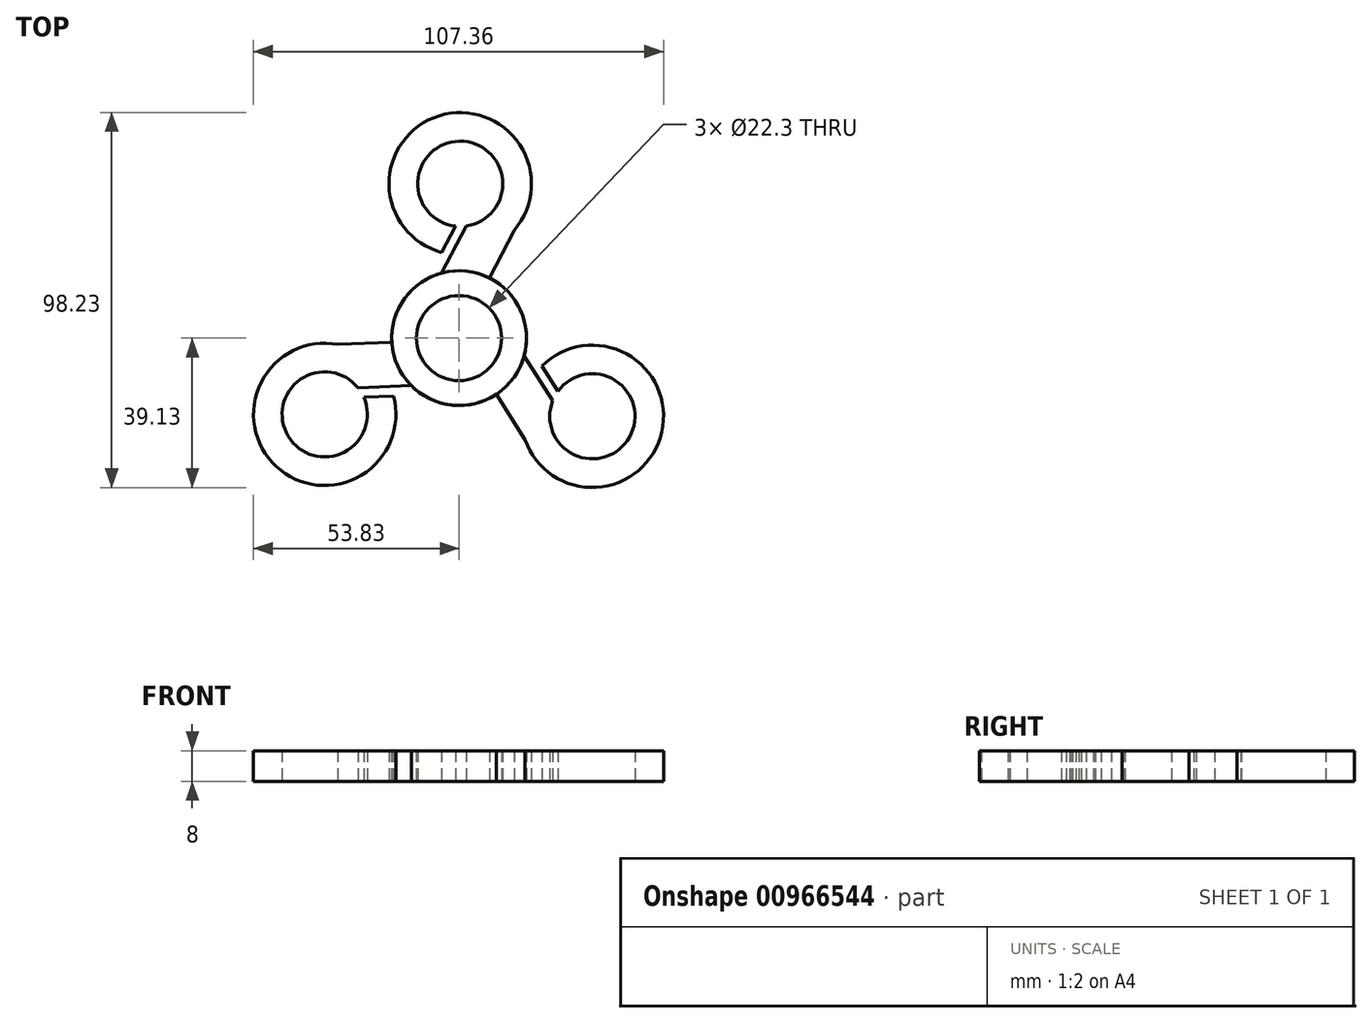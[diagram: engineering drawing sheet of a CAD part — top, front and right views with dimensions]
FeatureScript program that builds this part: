
annotation { "Feature Type Name" : "Feature", "Feature Type Description" : "" }
export const myFeature = defineFeature(function(context is Context, id is Id, definition is map)
    precondition{}
    {
        {
            var Q0;
            Q0=qCreatedBy(makeId("Top.planeOp"),FACE);
            var sketch = newSketch(context, id + "F0", { "sketchPlane" : qUnion([Q0])});
            skCircle(sketch, "E0", {"center": v(0, 0) * mm, "radius": 11.15 * mm});
            skCircle(sketch, "E1", {"center": v(0, 0) * mm, "radius": 17.65 * mm});
            skArc(sketch, "E2", {"start": v(14.43, 28.3) * mm, "mid": v(-5.2, 58.27) * mm, "end": v(-4.54, 22.44) * mm});
            skLineSegment(sketch, "E3", {"start": v(7.92, 15.77) * mm, "end": v(14.43, 28.3) * mm});
            skLineSegment(sketch, "E4", {"start": v(-4.54, 17.06) * mm, "end": v(-1.99, 21.95) * mm});
            skArc(sketch, "E5", {"start": v(1.9, 29.42) * mm, "mid": v(0.1, 51.6) * mm, "end": v(-0.93, 29.37) * mm});
            skLineSegment(sketch, "E6", {"start": v(-4.54, 22.44) * mm, "end": v(-0.93, 29.37) * mm});
            skLineSegment(sketch, "E7", {"start": v(-1.99, 21.95) * mm, "end": v(1.9, 29.42) * mm});
            skSolve(sketch);
        }
        {
            var Q0;
            Q0 = qSketchRegion(id + "F0", true);
            extrude(context, id + "F1", {"entities" : qUnion([Q0]), "depth" : 8 * mm, "offsetDistance" : 25.4 * mm});
        }
        {
            var Q0;
            Q0=qCreatedBy(makeId("Right.planeOp"),FACE);
            var sketch = newSketch(context, id + "F2", { "sketchPlane" : qUnion([Q0])});
            skLineSegment(sketch, "E8", {"start": v(0, 0) * mm, "end": v(0, 76.65) * mm});
            skSolve(sketch);
        }
        {
            var Q0;
            Q0=makeQuery(id+"F1.opExtrude","SWEPT_BODY",BODY,{"disambiguationData":[OSD([sQuery(id+"F0.wireOp",EDGE,"E0"),sQuery(id+"F0.wireOp",EDGE,"E1"),sQuery(id+"F0.wireOp",EDGE,"E2"),sQuery(id+"F0.wireOp",EDGE,"E3"),sQuery(id+"F0.wireOp",EDGE,"E4"),sQuery(id+"F0.wireOp",EDGE,"E5"),sQuery(id+"F0.wireOp",EDGE,"E6"),sQuery(id+"F0.wireOp",EDGE,"E7")])]});
            var Q1;
            Q1=sQuery(id+"F2.wireOp",EDGE,"E8");
            circularPattern(context, id + "F3", {"entities" : qUnion([Q0]), "axis" : qUnion([Q1]), "angle" : 360 * degree, "instanceCount" : 3, "equalSpace" : true});
        }
    });
